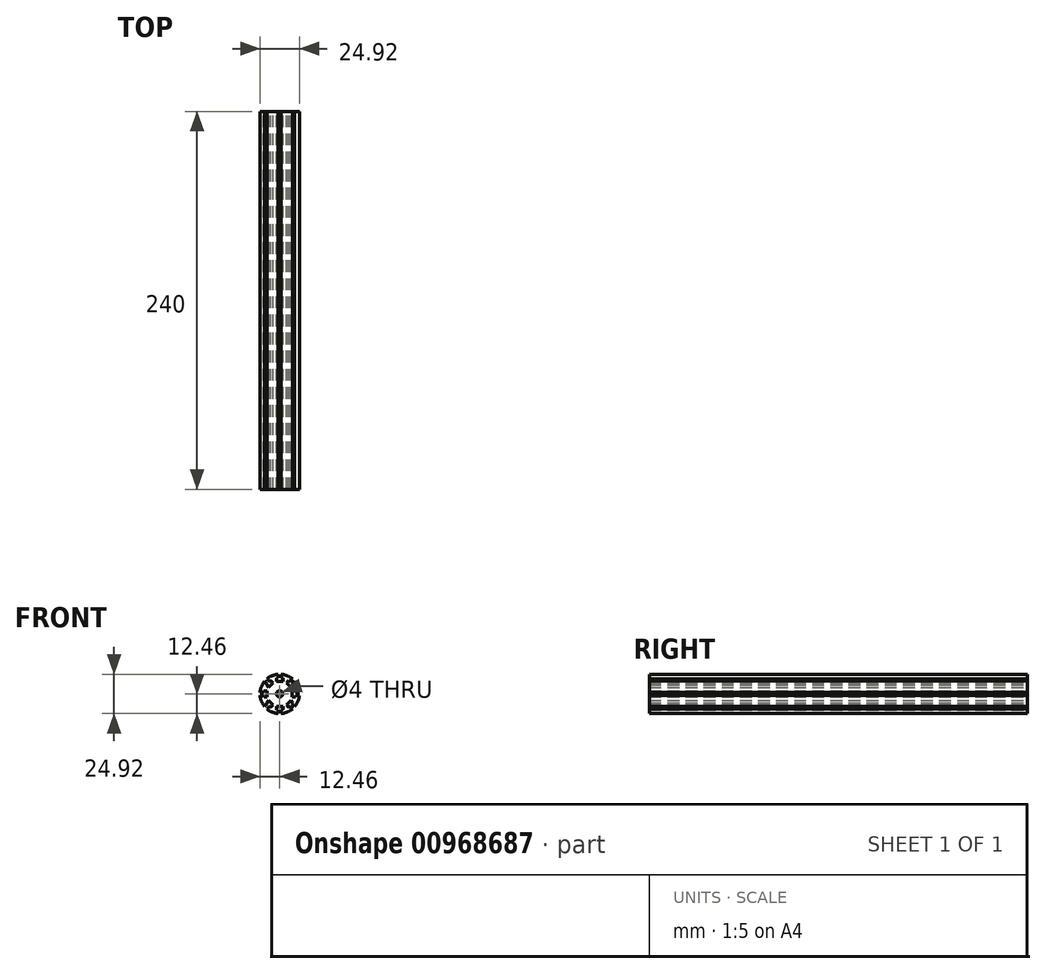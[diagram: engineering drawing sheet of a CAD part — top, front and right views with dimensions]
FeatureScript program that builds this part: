
annotation { "Feature Type Name" : "Feature", "Feature Type Description" : "" }
export const myFeature = defineFeature(function(context is Context, id is Id, definition is map)
    precondition{}
    {
        {
            var Q0;
            Q0=qCreatedBy(makeId("Front.planeOp"),FACE);
            var sketch = newSketch(context, id + "F0", { "sketchPlane" : qUnion([Q0])});
            skCircle(sketch, "E0", {"center": v(0, 0) * mm, "radius": 2 * mm});
            skLineSegment(sketch, "E1", {"start": v(8, 0) * mm, "end": v(8, -2) * mm});
            skLineSegment(sketch, "E2", {"start": v(8, -2) * mm, "end": v(10, -2) * mm});
            skLineSegment(sketch, "E3.MirrorCS", {"start": v(8, 0) * mm, "end": v(8, 2) * mm});
            skLineSegment(sketch, "E4.MirrorCS", {"start": v(8, 2) * mm, "end": v(10, 2) * mm});
            skArc(sketch, "E5", {"start": v(10.15, 1) * mm, "mid": v(10.09, 1.5) * mm, "end": v(10, 2) * mm});
            skLineSegment(sketch, "E6.MirrorCS", {"start": v(-8, 0) * mm, "end": v(-8, -2) * mm});
            skLineSegment(sketch, "E7.MirrorCS", {"start": v(-8, 0) * mm, "end": v(-8, 2) * mm});
            skLineSegment(sketch, "E8.MirrorCS", {"start": v(-8, 2) * mm, "end": v(-10, 2) * mm});
            skLineSegment(sketch, "E9.MirrorCS", {"start": v(-8, -2) * mm, "end": v(-10, -2) * mm});
            skArc(sketch, "E10", {"start": v(12.46, 1) * mm, "mid": v(11.55, 4.78) * mm, "end": v(9.52, 8.1) * mm});
            skLineSegment(sketch, "E11", {"start": v(10.15, 1) * mm, "end": v(12.46, 1) * mm});
            skLineSegment(sketch, "E12", {"start": v(10.15, -1) * mm, "end": v(12.46, -1) * mm});
            skPoint(sketch, "E13.orphan", {"position": v(8, 1) * mm});
            skPoint(sketch, "E14.orphan", {"position": v(8, -1) * mm});
            skPoint(sketch, "E15.orphan", {"position": v(13.82, 1) * mm});
            skPoint(sketch, "E16.orphan", {"position": v(13.82, -1) * mm});
            skLineSegment(sketch, "E17.MirrorCS", {"start": v(-10.15, -1) * mm, "end": v(-12.46, -1) * mm});
            skLineSegment(sketch, "E18.MirrorCS", {"start": v(-10.15, 1) * mm, "end": v(-12.46, 1) * mm});
            skArc(sketch, "E19.trimOffspring", {"start": v(-10.15, -1) * mm, "mid": v(-10.09, -1.5) * mm, "end": v(-10, -2) * mm});
            skArc(sketch, "E20.trimOffspring", {"start": v(-12.46, -1) * mm, "mid": v(-11.55, -4.78) * mm, "end": v(-9.52, -8.1) * mm});
            skArc(sketch, "E21.trimOffspring", {"start": v(-10, 2) * mm, "mid": v(-10.09, 1.5) * mm, "end": v(-10.15, 1) * mm});
            skArc(sketch, "E22.trimOffspring", {"start": v(10, -2) * mm, "mid": v(10.09, -1.5) * mm, "end": v(10.15, -1) * mm});
            skLineSegment(sketch, "E23.MirrorCS", {"start": v(1, 10.15) * mm, "end": v(1, 12.46) * mm});
            skLineSegment(sketch, "E24.MirrorCS", {"start": v(-1, 10.15) * mm, "end": v(-1, 12.46) * mm});
            skArc(sketch, "E25.MirrorCS", {"start": v(1, 10.15) * mm, "mid": v(1.5, 10.09) * mm, "end": v(2, 10) * mm});
            skArc(sketch, "E26.MirrorCS", {"start": v(-2, 10) * mm, "mid": v(-1.5, 10.09) * mm, "end": v(-1, 10.15) * mm});
            skLineSegment(sketch, "E27.MirrorCS", {"start": v(-2, 8) * mm, "end": v(-2, 10) * mm});
            skLineSegment(sketch, "E28.MirrorCS", {"start": v(0, 8) * mm, "end": v(-2, 8) * mm});
            skLineSegment(sketch, "E29.MirrorCS", {"start": v(0, 8) * mm, "end": v(2, 8) * mm});
            skLineSegment(sketch, "E30.MirrorCS", {"start": v(2, 8) * mm, "end": v(2, 10) * mm});
            skLineSegment(sketch, "E31.MirrorCS", {"start": v(2, -8) * mm, "end": v(2, -10) * mm});
            skLineSegment(sketch, "E32.MirrorCS", {"start": v(0, -8) * mm, "end": v(2, -8) * mm});
            skLineSegment(sketch, "E33.MirrorCS", {"start": v(-2, -8) * mm, "end": v(-2, -10) * mm});
            skArc(sketch, "E34.MirrorCS", {"start": v(-1, -10.15) * mm, "mid": v(-1.5, -10.09) * mm, "end": v(-2, -10) * mm});
            skArc(sketch, "E35.MirrorCS", {"start": v(2, -10) * mm, "mid": v(1.5, -10.09) * mm, "end": v(1, -10.15) * mm});
            skLineSegment(sketch, "E36.MirrorCS", {"start": v(1, -10.15) * mm, "end": v(1, -12.46) * mm});
            skLineSegment(sketch, "E37.MirrorCS", {"start": v(-1, -10.15) * mm, "end": v(-1, -12.46) * mm});
            skLineSegment(sketch, "E38.MirrorCS", {"start": v(0, -8) * mm, "end": v(-2, -8) * mm});
            skArc(sketch, "E39.trimOffspring", {"start": v(-1, 12.46) * mm, "mid": v(-4.78, 11.55) * mm, "end": v(-8.1, 9.52) * mm});
            skArc(sketch, "E40.trimOffspring", {"start": v(1, -12.46) * mm, "mid": v(4.78, -11.55) * mm, "end": v(8.1, -9.52) * mm});
            skLineSegment(sketch, "E41.MirrorCS", {"start": v(-5.66, -5.66) * mm, "end": v(-4.24, -7.07) * mm});
            skLineSegment(sketch, "E42.MirrorCS", {"start": v(-5.66, -5.66) * mm, "end": v(-7.07, -4.24) * mm});
            skLineSegment(sketch, "E43.MirrorCS", {"start": v(-4.24, -7.07) * mm, "end": v(-5.66, -8.49) * mm});
            skArc(sketch, "E44.MirrorCS", {"start": v(-6.47, -7.88) * mm, "mid": v(-6.07, -8.2) * mm, "end": v(-5.66, -8.49) * mm});
            skLineSegment(sketch, "E45.MirrorCS", {"start": v(-6.47, -7.88) * mm, "end": v(-8.1, -9.52) * mm});
            skLineSegment(sketch, "E46.MirrorCS", {"start": v(-7.88, -6.47) * mm, "end": v(-9.52, -8.1) * mm});
            skArc(sketch, "E47.MirrorCS", {"start": v(-8.49, -5.66) * mm, "mid": v(-8.2, -6.07) * mm, "end": v(-7.88, -6.47) * mm});
            skLineSegment(sketch, "E48.MirrorCS", {"start": v(-7.07, -4.24) * mm, "end": v(-8.49, -5.66) * mm});
            skLineSegment(sketch, "E49.MirrorCS", {"start": v(-7.07, 4.24) * mm, "end": v(-8.49, 5.66) * mm});
            skArc(sketch, "E50.MirrorCS", {"start": v(-8.49, 5.66) * mm, "mid": v(-8.2, 6.07) * mm, "end": v(-7.88, 6.47) * mm});
            skLineSegment(sketch, "E51.MirrorCS", {"start": v(-7.88, 6.47) * mm, "end": v(-9.52, 8.1) * mm});
            skLineSegment(sketch, "E52.MirrorCS", {"start": v(-6.47, 7.88) * mm, "end": v(-8.1, 9.52) * mm});
            skArc(sketch, "E53.MirrorCS", {"start": v(-6.47, 7.88) * mm, "mid": v(-6.07, 8.2) * mm, "end": v(-5.66, 8.49) * mm});
            skLineSegment(sketch, "E54.MirrorCS", {"start": v(-4.24, 7.07) * mm, "end": v(-5.66, 8.49) * mm});
            skLineSegment(sketch, "E55.MirrorCS", {"start": v(-5.66, 5.66) * mm, "end": v(-4.24, 7.07) * mm});
            skLineSegment(sketch, "E56.MirrorCS", {"start": v(-5.66, 5.66) * mm, "end": v(-7.07, 4.24) * mm});
            skLineSegment(sketch, "E57.MirrorCS", {"start": v(6.47, 7.88) * mm, "end": v(8.1, 9.52) * mm});
            skArc(sketch, "E58.MirrorCS", {"start": v(6.47, 7.88) * mm, "mid": v(6.07, 8.2) * mm, "end": v(5.66, 8.49) * mm});
            skLineSegment(sketch, "E59.MirrorCS", {"start": v(4.24, 7.07) * mm, "end": v(5.66, 8.49) * mm});
            skLineSegment(sketch, "E60.MirrorCS", {"start": v(5.66, 5.66) * mm, "end": v(4.24, 7.07) * mm});
            skLineSegment(sketch, "E61.MirrorCS", {"start": v(5.66, 5.66) * mm, "end": v(7.07, 4.24) * mm});
            skLineSegment(sketch, "E62.MirrorCS", {"start": v(7.07, 4.24) * mm, "end": v(8.49, 5.66) * mm});
            skArc(sketch, "E63.MirrorCS", {"start": v(8.49, 5.66) * mm, "mid": v(8.2, 6.07) * mm, "end": v(7.88, 6.47) * mm});
            skLineSegment(sketch, "E64.MirrorCS", {"start": v(7.88, 6.47) * mm, "end": v(9.52, 8.1) * mm});
            skLineSegment(sketch, "E65.MirrorCS", {"start": v(7.07, -4.24) * mm, "end": v(8.49, -5.66) * mm});
            skLineSegment(sketch, "E66.MirrorCS", {"start": v(5.66, -5.66) * mm, "end": v(4.24, -7.07) * mm});
            skLineSegment(sketch, "E67.MirrorCS", {"start": v(5.66, -5.66) * mm, "end": v(7.07, -4.24) * mm});
            skLineSegment(sketch, "E68.MirrorCS", {"start": v(4.24, -7.07) * mm, "end": v(5.66, -8.49) * mm});
            skArc(sketch, "E69.MirrorCS", {"start": v(6.47, -7.88) * mm, "mid": v(6.07, -8.2) * mm, "end": v(5.66, -8.49) * mm});
            skArc(sketch, "E70.MirrorCS", {"start": v(8.49, -5.66) * mm, "mid": v(8.2, -6.07) * mm, "end": v(7.88, -6.47) * mm});
            skLineSegment(sketch, "E71.MirrorCS", {"start": v(7.88, -6.47) * mm, "end": v(9.52, -8.1) * mm});
            skLineSegment(sketch, "E72.MirrorCS", {"start": v(6.47, -7.88) * mm, "end": v(8.1, -9.52) * mm});
            skArc(sketch, "E73.trimOffspring", {"start": v(-9.52, 8.1) * mm, "mid": v(-11.55, 4.78) * mm, "end": v(-12.46, 1) * mm});
            skArc(sketch, "E74.trimOffspring", {"start": v(8.1, 9.52) * mm, "mid": v(4.78, 11.55) * mm, "end": v(1, 12.46) * mm});
            skArc(sketch, "E75.trimOffspring", {"start": v(9.52, -8.1) * mm, "mid": v(11.55, -4.78) * mm, "end": v(12.46, -1) * mm});
            skArc(sketch, "E76.trimOffspring", {"start": v(-8.1, -9.52) * mm, "mid": v(-4.78, -11.55) * mm, "end": v(-1, -12.46) * mm});
            skPoint(sketch, "E77.start.orphan", {"position": v(-0.7, -1.7) * mm});
            skPoint(sketch, "E78.orphan", {"position": v(-1.41, -1.41) * mm});
            skPoint(sketch, "E79.start.orphan", {"position": v(-2, -2) * mm});
            skPoint(sketch, "E80.end.orphan", {"position": v(0, -2) * mm});
            skSolve(sketch);
        }
        {
            var Q0;
            Q0 = qSketchRegion(id + "F0", true);
            extrude(context, id + "F1", {"entities" : qUnion([Q0]), "depth" : 100 * mm, "offsetDistance" : 25 * mm});
        }
        {
            var Q0;
            Q0=makeQuery(id+"F1.opExtrude","CAP_FACE",FACE,{"disambiguationData":[OSD([sQuery(id+"F0.wireOp",EDGE,"E0"),sQuery(id+"F0.wireOp",EDGE,"E1"),sQuery(id+"F0.wireOp",EDGE,"E2"),sQuery(id+"F0.wireOp",EDGE,"E3.MirrorCS"),sQuery(id+"F0.wireOp",EDGE,"E4.MirrorCS"),sQuery(id+"F0.wireOp",EDGE,"E5"),sQuery(id+"F0.wireOp",EDGE,"E6.MirrorCS"),sQuery(id+"F0.wireOp",EDGE,"E7.MirrorCS"),sQuery(id+"F0.wireOp",EDGE,"E8.MirrorCS"),sQuery(id+"F0.wireOp",EDGE,"E9.MirrorCS"),sQuery(id+"F0.wireOp",EDGE,"E10"),sQuery(id+"F0.wireOp",EDGE,"E11"),sQuery(id+"F0.wireOp",EDGE,"E12"),sQuery(id+"F0.wireOp",EDGE,"E17.MirrorCS"),sQuery(id+"F0.wireOp",EDGE,"E18.MirrorCS"),sQuery(id+"F0.wireOp",EDGE,"E19.trimOffspring"),sQuery(id+"F0.wireOp",EDGE,"E20.trimOffspring"),sQuery(id+"F0.wireOp",EDGE,"E21.trimOffspring"),sQuery(id+"F0.wireOp",EDGE,"E22.trimOffspring"),sQuery(id+"F0.wireOp",EDGE,"E23.MirrorCS"),sQuery(id+"F0.wireOp",EDGE,"E24.MirrorCS"),sQuery(id+"F0.wireOp",EDGE,"E25.MirrorCS"),sQuery(id+"F0.wireOp",EDGE,"E26.MirrorCS"),sQuery(id+"F0.wireOp",EDGE,"E27.MirrorCS"),sQuery(id+"F0.wireOp",EDGE,"E28.MirrorCS"),sQuery(id+"F0.wireOp",EDGE,"E29.MirrorCS"),sQuery(id+"F0.wireOp",EDGE,"E30.MirrorCS"),sQuery(id+"F0.wireOp",EDGE,"E31.MirrorCS"),sQuery(id+"F0.wireOp",EDGE,"E32.MirrorCS"),sQuery(id+"F0.wireOp",EDGE,"E33.MirrorCS"),sQuery(id+"F0.wireOp",EDGE,"E34.MirrorCS"),sQuery(id+"F0.wireOp",EDGE,"E35.MirrorCS"),sQuery(id+"F0.wireOp",EDGE,"E36.MirrorCS"),sQuery(id+"F0.wireOp",EDGE,"E37.MirrorCS"),sQuery(id+"F0.wireOp",EDGE,"E38.MirrorCS"),sQuery(id+"F0.wireOp",EDGE,"E39.trimOffspring"),sQuery(id+"F0.wireOp",EDGE,"E40.trimOffspring"),sQuery(id+"F0.wireOp",EDGE,"E41.MirrorCS"),sQuery(id+"F0.wireOp",EDGE,"E42.MirrorCS"),sQuery(id+"F0.wireOp",EDGE,"E43.MirrorCS"),sQuery(id+"F0.wireOp",EDGE,"E44.MirrorCS"),sQuery(id+"F0.wireOp",EDGE,"E45.MirrorCS"),sQuery(id+"F0.wireOp",EDGE,"E46.MirrorCS"),sQuery(id+"F0.wireOp",EDGE,"E47.MirrorCS"),sQuery(id+"F0.wireOp",EDGE,"E48.MirrorCS"),sQuery(id+"F0.wireOp",EDGE,"E49.MirrorCS"),sQuery(id+"F0.wireOp",EDGE,"E50.MirrorCS"),sQuery(id+"F0.wireOp",EDGE,"E51.MirrorCS"),sQuery(id+"F0.wireOp",EDGE,"E52.MirrorCS"),sQuery(id+"F0.wireOp",EDGE,"E53.MirrorCS"),sQuery(id+"F0.wireOp",EDGE,"E54.MirrorCS"),sQuery(id+"F0.wireOp",EDGE,"E55.MirrorCS"),sQuery(id+"F0.wireOp",EDGE,"E56.MirrorCS"),sQuery(id+"F0.wireOp",EDGE,"E57.MirrorCS"),sQuery(id+"F0.wireOp",EDGE,"E58.MirrorCS"),sQuery(id+"F0.wireOp",EDGE,"E59.MirrorCS"),sQuery(id+"F0.wireOp",EDGE,"E60.MirrorCS"),sQuery(id+"F0.wireOp",EDGE,"E61.MirrorCS"),sQuery(id+"F0.wireOp",EDGE,"E62.MirrorCS"),sQuery(id+"F0.wireOp",EDGE,"E63.MirrorCS"),sQuery(id+"F0.wireOp",EDGE,"E64.MirrorCS"),sQuery(id+"F0.wireOp",EDGE,"E65.MirrorCS"),sQuery(id+"F0.wireOp",EDGE,"E66.MirrorCS"),sQuery(id+"F0.wireOp",EDGE,"E67.MirrorCS"),sQuery(id+"F0.wireOp",EDGE,"E68.MirrorCS"),sQuery(id+"F0.wireOp",EDGE,"E69.MirrorCS"),sQuery(id+"F0.wireOp",EDGE,"E70.MirrorCS"),sQuery(id+"F0.wireOp",EDGE,"E71.MirrorCS"),sQuery(id+"F0.wireOp",EDGE,"E72.MirrorCS"),sQuery(id+"F0.wireOp",EDGE,"E73.trimOffspring"),sQuery(id+"F0.wireOp",EDGE,"E74.trimOffspring"),sQuery(id+"F0.wireOp",EDGE,"E75.trimOffspring"),sQuery(id+"F0.wireOp",EDGE,"E76.trimOffspring")])],"isStart":false});
            extrude(context, id + "F2", {"entities" : qUnion([Q0]), "operationType" : NewBodyOperationType.ADD, "depth" : 140 * mm, "offsetDistance" : 25 * mm});
        }
    });
